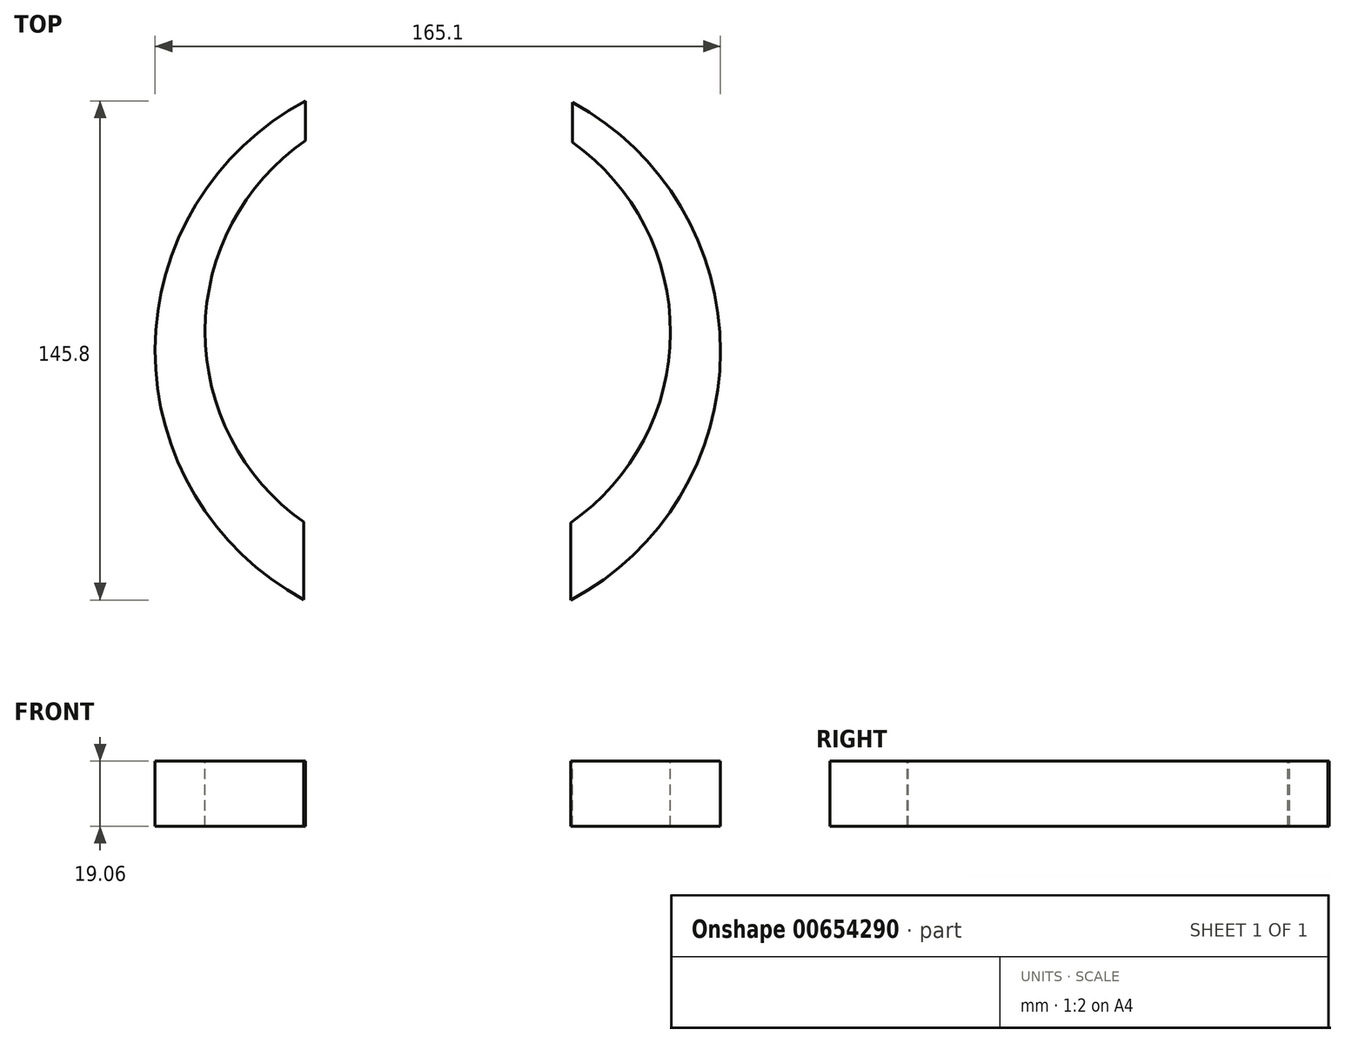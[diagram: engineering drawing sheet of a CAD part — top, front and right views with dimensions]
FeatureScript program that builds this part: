
annotation { "Feature Type Name" : "Feature", "Feature Type Description" : "" }
export const myFeature = defineFeature(function(context is Context, id is Id, definition is map)
    precondition{}
    {
        {
            var Q0;
            Q0=qCreatedBy(makeId("Top.planeOp"),FACE);
            var sketch = newSketch(context, id + "F0", { "sketchPlane" : qUnion([Q0])});
            skCircle(sketch, "E0", {"center": v(0, 0) * mm, "radius": 82.55 * mm});
            skSolve(sketch);
        }
        {
            var Q0;
            Q0=qSketchRegion(id+"F0",true);
            extrude(context, id + "F1", {"entities" : qUnion([Q0]), "endBound" : BoundingType.SYMMETRIC, "depth" : 19.05 * mm, "offsetDistance" : 25.4 * mm});
        }
        {
            var Q0;
            Q0=qCreatedBy(makeId("Top.planeOp"),FACE);
            var sketch = newSketch(context, id + "F2", { "sketchPlane" : qUnion([Q0])});
            skLineSegment(sketch, "E1.top", {"start": v(12.07, -82.62) * mm, "end": v(-12.06, -82.62) * mm});
            skPoint(sketch, "E1.middle", {"position": v(0, 0) * mm});
            skLineSegment(sketch, "E2", {"start": v(-12.06, 16.82) * mm, "end": v(12.07, 16.82) * mm});
            skLineSegment(sketch, "E3", {"start": v(-12.06, 16.82) * mm, "end": v(-12.06, -82.62) * mm});
            skLineSegment(sketch, "E4", {"start": v(12.07, 16.82) * mm, "end": v(12.07, -82.62) * mm});
            skSolve(sketch);
        }
        {
            var Q0;
            Q0=qSketchRegion(id+"F2",true);
            extrude(context, id + "F3", {"entities" : qUnion([Q0]), "operationType" : NewBodyOperationType.REMOVE, "endBound" : BoundingType.SYMMETRIC, "oppositeDirection" : true, "depth" : 19.05 * mm, "offsetDistance" : 25.4 * mm});
        }
        {
            var Q0;
            Q0=makeQuery(id+"F1.opExtrude","CAP_FACE",FACE,{"disambiguationData":[OSD([sQuery(id+"F0.wireOp",EDGE,"E0")])],"isStart":false});
            var sketch = newSketch(context, id + "F4", { "sketchPlane" : qUnion([Q0])});
            skCircle(sketch, "E5", {"center": v(0, 5.51) * mm, "radius": 67.95 * mm});
            skSolve(sketch);
        }
        {
            var Q0;
            Q0=qSketchRegion(id+"F4",true);
            extrude(context, id + "F5", {"entities" : qUnion([Q0]), "operationType" : NewBodyOperationType.REMOVE, "oppositeDirection" : true, "depth" : 19.05 * mm, "offsetDistance" : 25.4 * mm});
        }
        {
            var Q0;
            Q0=qCreatedBy(makeId("Top.planeOp"),FACE);
            var Q1;
            Q1=qCreatedBy(makeId("Top.planeOp"),FACE);
            var sketch = newSketch(context, id + "F6", { "sketchPlane" : qUnion([Q0, Q1])});
            skLineSegment(sketch, "E6", {"start": v(-5.84, -40.27) * mm, "end": v(-39.12, -40.27) * mm});
            skLineSegment(sketch, "E7", {"start": v(-39.12, -40.27) * mm, "end": v(-39.12, -91.07) * mm});
            skLineSegment(sketch, "E8", {"start": v(-39.12, -91.07) * mm, "end": v(38.86, -91.07) * mm});
            skLineSegment(sketch, "E9", {"start": v(38.86, -91.07) * mm, "end": v(38.86, -40.27) * mm});
            skLineSegment(sketch, "E10", {"start": v(38.86, -40.27) * mm, "end": v(-5.84, -40.27) * mm});
            skSolve(sketch);
        }
        {
            var Q0;
            Q0 = qSketchRegion(id + "F6", true);
            extrude(context, id + "F7", {"entities" : qUnion([Q0]), "operationType" : NewBodyOperationType.REMOVE, "endBound" : BoundingType.SYMMETRIC, "oppositeDirection" : true, "depth" : 19.05 * mm, "offsetDistance" : 25.4 * mm});
        }
        {
            var Q0;
            Q0=qCreatedBy(makeId("Top.planeOp"),FACE);
            var sketch = newSketch(context, id + "F8", { "sketchPlane" : qUnion([Q0])});
            skLineSegment(sketch, "E11", {"start": v(6.1, 102.52) * mm, "end": v(-38.6, 102.52) * mm});
            skLineSegment(sketch, "E12", {"start": v(-38.6, 102.52) * mm, "end": v(-38.6, 51.72) * mm});
            skLineSegment(sketch, "E13", {"start": v(-38.6, 51.72) * mm, "end": v(6.1, 51.72) * mm});
            skLineSegment(sketch, "E14", {"start": v(6.1, 51.72) * mm, "end": v(39.37, 51.72) * mm});
            skLineSegment(sketch, "E15", {"start": v(39.37, 51.72) * mm, "end": v(39.37, 102.8) * mm});
            skLineSegment(sketch, "E16", {"start": v(39.37, 102.8) * mm, "end": v(6.1, 102.52) * mm});
            skSolve(sketch);
        }
        {
            var Q0;
            Q0 = qSketchRegion(id + "F8", true);
            extrude(context, id + "F9", {"entities" : qUnion([Q0]), "operationType" : NewBodyOperationType.REMOVE, "endBound" : BoundingType.SYMMETRIC, "oppositeDirection" : true, "depth" : 44.45 * mm, "offsetDistance" : 25.4 * mm});
        }
    });
